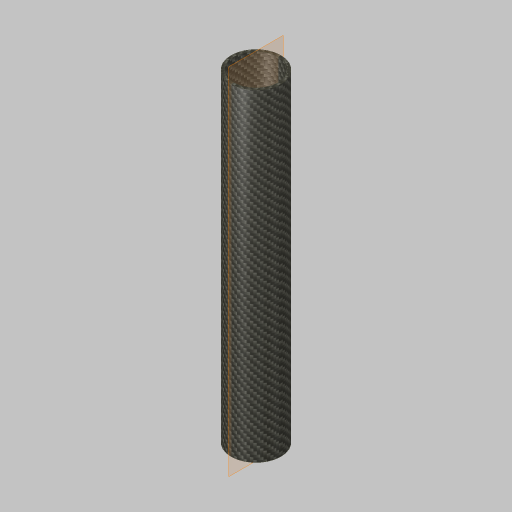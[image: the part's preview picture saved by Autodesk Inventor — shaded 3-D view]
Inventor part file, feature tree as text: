
AUTODESK INVENTOR PART (.ipt)
format: ipt  version: 2023.5 (Build 275446000, 446)  size: 144,384 bytes
history: native  units: in
note: dims shown in document units (in); Inventor stores cm internally (conversion verified against a paired STEP export)
features: extrude x1, sketch x1
ambient origin geometry x8: Origin, YZ Plane, XZ Plane, XY Plane, X Axis, Y Axis, Z Axis, Center Point
bodies: Solid1 (feature_tree)
feature tree (2):
  extrude  "Extrusion1"  Depth=13.0in
  sketch  "Sketch1"  dims[d0=2.0in d1=0.1in d2=13.0in d3=0.0in]
